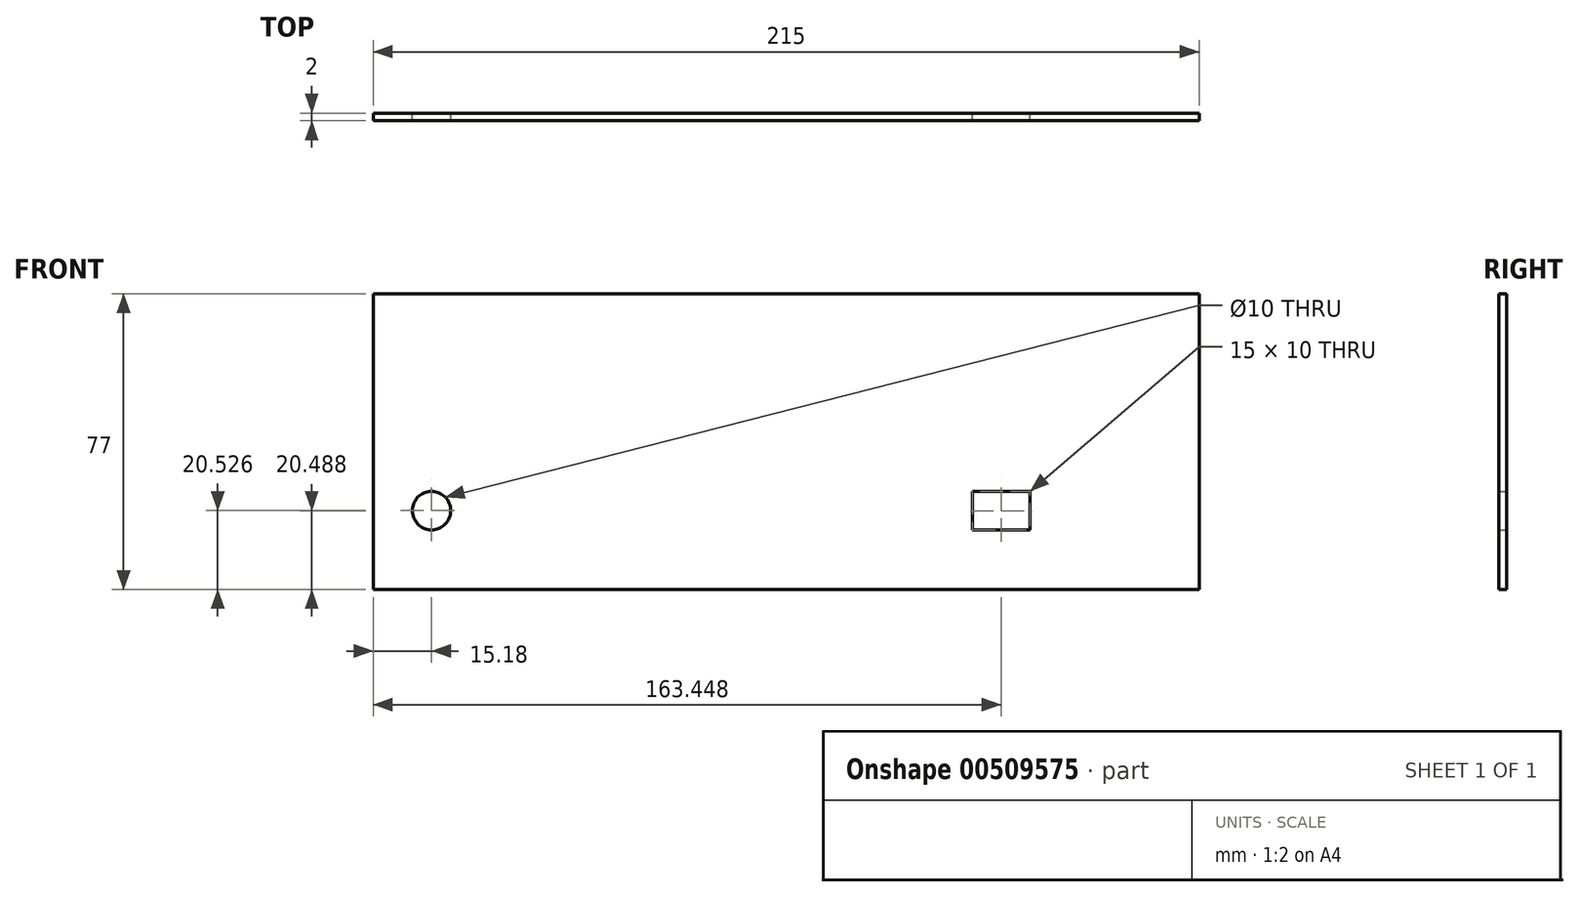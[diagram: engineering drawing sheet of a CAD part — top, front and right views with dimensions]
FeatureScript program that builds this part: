
annotation { "Feature Type Name" : "Feature", "Feature Type Description" : "" }
export const myFeature = defineFeature(function(context is Context, id is Id, definition is map)
    precondition{}
    {
        {
            var Q0;
            Q0=qCreatedBy(makeId("Front.planeOp"),FACE);
            var sketch = newSketch(context, id + "F0", { "sketchPlane" : qUnion([Q0])});
            skLineSegment(sketch, "E0.bottom", {"start": v(0, 0) * mm, "end": v(215, 0) * mm});
            skLineSegment(sketch, "E0.top", {"start": v(0, 77) * mm, "end": v(215, 77) * mm});
            skLineSegment(sketch, "E0.left", {"start": v(0, 0) * mm, "end": v(0, 77) * mm});
            skLineSegment(sketch, "E0.right", {"start": v(215, 0) * mm, "end": v(215, 77) * mm});
            skCircle(sketch, "E1", {"center": v(15.18, 20.53) * mm, "radius": 5 * mm});
            skLineSegment(sketch, "E2.bottom", {"start": v(155.95, 25.49) * mm, "end": v(170.95, 25.49) * mm});
            skLineSegment(sketch, "E2.top", {"start": v(155.95, 15.49) * mm, "end": v(170.95, 15.49) * mm});
            skLineSegment(sketch, "E2.left", {"start": v(155.95, 25.49) * mm, "end": v(155.95, 15.49) * mm});
            skLineSegment(sketch, "E2.right", {"start": v(170.95, 25.49) * mm, "end": v(170.95, 15.49) * mm});
            skSolve(sketch);
        }
        {
            var Q0;
            Q0=makeQuery(id+"F0.imprint","IMPRINT",FACE,{"disambiguationData":[TD([[makeQuery(id+"F0.imprint","IMPRINT",EDGE,{"derivedFrom":sQuery(id+"F0.wireOp",EDGE,"E0.bottom")}),1.0]])]});
            extrude(context, id + "F1", {"entities" : qUnion([Q0]), "endBound" : BoundingType.SYMMETRIC, "depth" : 2 * mm});
        }
    });
